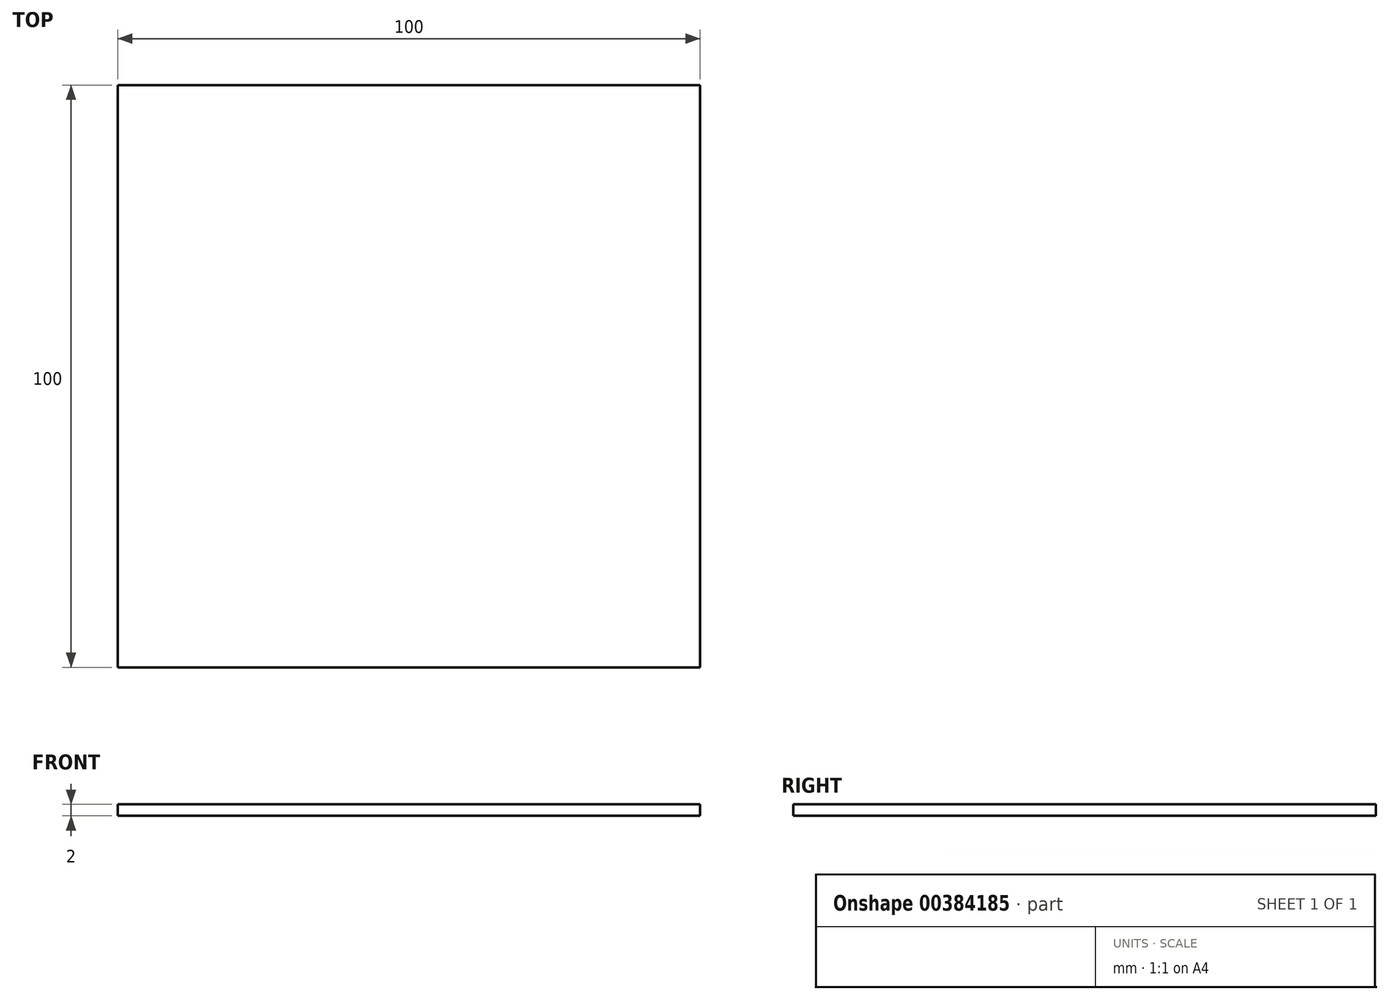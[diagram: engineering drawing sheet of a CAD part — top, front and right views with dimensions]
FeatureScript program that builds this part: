
annotation { "Feature Type Name" : "Feature", "Feature Type Description" : "" }
export const myFeature = defineFeature(function(context is Context, id is Id, definition is map)
    precondition{}
    {
        {
            var Q0;
            Q0=qCreatedBy(makeId("Top.planeOp"),FACE);
            var sketch = newSketch(context, id + "F0", { "sketchPlane" : qUnion([Q0])});
            skLineSegment(sketch, "E0.bottom", {"start": v(0, 0) * mm, "end": v(-100, 0) * mm});
            skLineSegment(sketch, "E0.top", {"start": v(0, 100) * mm, "end": v(-100, 100) * mm});
            skLineSegment(sketch, "E0.left", {"start": v(0, 0) * mm, "end": v(0, 100) * mm});
            skLineSegment(sketch, "E0.right", {"start": v(-100, 0) * mm, "end": v(-100, 100) * mm});
            skSolve(sketch);
        }
        {
            var Q0;
            Q0 = qSketchRegion(id + "F0", true);
            var Q1;
            Q1=makeQuery(id+"F0.imprint","IMPRINT",FACE,{"disambiguationData":[TD([[makeQuery(id+"F0.imprint","IMPRINT",EDGE,{"derivedFrom":sQuery(id+"F0.wireOp",EDGE,"E0.bottom")}),-1.0]])]});
            extrude(context, id + "F1", {"entities" : qUnion([Q0, Q1]), "depth" : 2 * mm});
        }
    });
